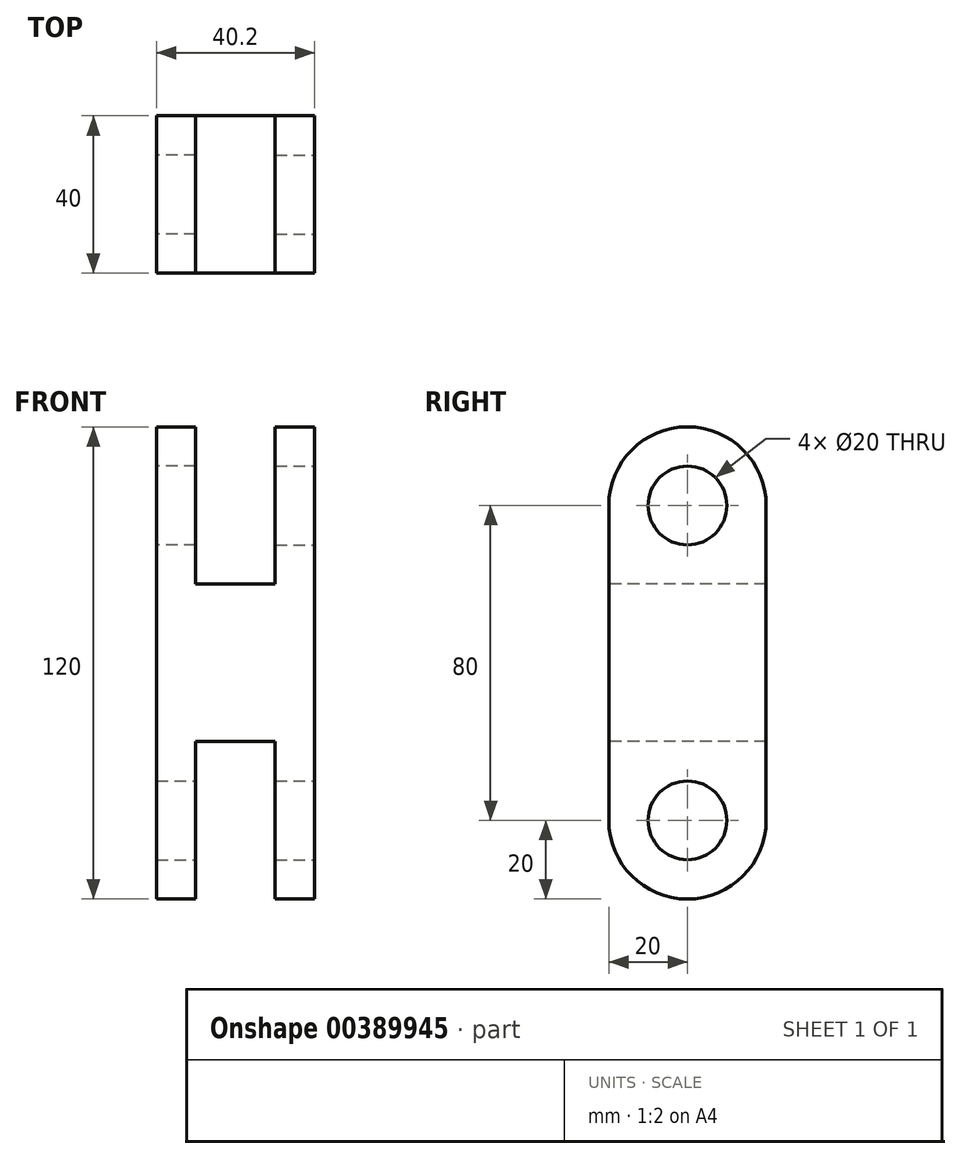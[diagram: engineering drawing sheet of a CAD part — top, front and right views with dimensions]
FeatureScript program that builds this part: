
annotation { "Feature Type Name" : "Feature", "Feature Type Description" : "" }
export const myFeature = defineFeature(function(context is Context, id is Id, definition is map)
    precondition{}
    {
        {
            var Q0;
            Q0=qCreatedBy(makeId("Right.planeOp"),FACE);
            var sketch = newSketch(context, id + "F0", { "sketchPlane" : qUnion([Q0])});
            skLineSegment(sketch, "E0.bottom", {"start": v(20, 40) * mm, "end": v(-20, 40) * mm});
            skLineSegment(sketch, "E0.top", {"start": v(20, -40) * mm, "end": v(-20, -40) * mm});
            skLineSegment(sketch, "E0.left", {"start": v(20, 40) * mm, "end": v(20, -40) * mm});
            skLineSegment(sketch, "E0.right", {"start": v(-20, 40) * mm, "end": v(-20, -40) * mm});
            skPoint(sketch, "E0.middle", {"position": v(0, 0) * mm});
            skSolve(sketch);
        }
        {
            var Q0;
            Q0 = qSketchRegion(id + "F0", true);
            extrude(context, id + "F1", {"entities" : qUnion([Q0]), "depth" : 20.1 * mm});
        }
        {
            var Q0;
            Q0=makeQuery(id+"F1.opExtrude","CAP_FACE",FACE,{"disambiguationData":[OSD([sQuery(id+"F0.wireOp",EDGE,"E0.bottom"),sQuery(id+"F0.wireOp",EDGE,"E0.top"),sQuery(id+"F0.wireOp",EDGE,"E0.left"),sQuery(id+"F0.wireOp",EDGE,"E0.right")])],"isStart":false});
            var sketch = newSketch(context, id + "F2", { "sketchPlane" : qUnion([Q0])});
            skLineSegment(sketch, "E1.bottom", {"start": v(-20, 40) * mm, "end": v(20, 40) * mm});
            skLineSegment(sketch, "E1.left", {"start": v(-20, 40) * mm, "end": v(-20, 60) * mm});
            skLineSegment(sketch, "E1.right", {"start": v(20, 40) * mm, "end": v(20, 60) * mm});
            skArc(sketch, "E2", {"start": v(20, 60) * mm, "mid": v(0, 80) * mm, "end": v(-20, 60) * mm});
            skCircle(sketch, "E3", {"center": v(0, 60) * mm, "radius": 10 * mm});
            skSolve(sketch);
        }
        {
            var Q0;
            Q0 = qSketchRegion(id + "F2", true);
            extrude(context, id + "F3", {"entities" : qUnion([Q0]), "operationType" : NewBodyOperationType.ADD, "oppositeDirection" : true, "depth" : 10 * mm});
        }
        {
            var Q0;
            Q0=makeQuery(id+"F1.opExtrude","SWEPT_BODY",BODY,{"disambiguationData":[OSD([sQuery(id+"F0.wireOp",EDGE,"E0.bottom"),sQuery(id+"F0.wireOp",EDGE,"E0.top"),sQuery(id+"F0.wireOp",EDGE,"E0.left"),sQuery(id+"F0.wireOp",EDGE,"E0.right")])]});
            var Q1;
            Q1=qCreatedBy(makeId("Right.planeOp"),FACE);
            mirror(context, id + "F4", {"operationType" : NewBodyOperationType.ADD, "entities" : qUnion([Q0]), "mirrorPlane" : qUnion([Q1])});
        }
        {
            var Q0;
            {var subQ0=makeQuery(id+"F3.boolean.opBoolean","MERGE",FACE,{"derivedFrom":[makeQuery(id+"F1.opExtrude","SWEPT_FACE",FACE,{"disambiguationData":[OSD([sQuery(id+"F0.wireOp",EDGE,"E0.right")])]}),makeQuery(id+"F3.opExtrude","SWEPT_FACE",FACE,{"disambiguationData":[OSD([sQuery(id+"F2.wireOp",EDGE,"E1.left")])]})]});Q0=makeQuery(id+"F4.boolean.opBoolean","MERGE",FACE,{"derivedFrom":[subQ0,makeQuery(id+"F4.opPattern","COPY",FACE,{"derivedFrom":subQ0,"instanceName":"1"})]});}
            var sketch = newSketch(context, id + "F5", { "sketchPlane" : qUnion([Q0])});
            skLineSegment(sketch, "E4.bottom", {"start": v(-10.1, -40) * mm, "end": v(10.1, -40) * mm});
            skLineSegment(sketch, "E4.top", {"start": v(-10.1, 0) * mm, "end": v(10.1, 0) * mm});
            skLineSegment(sketch, "E4.left", {"start": v(-10.1, -40) * mm, "end": v(-10.1, 0) * mm});
            skLineSegment(sketch, "E4.right", {"start": v(10.1, -40) * mm, "end": v(10.1, 0) * mm});
            skSolve(sketch);
        }
        {
            var Q0;
            Q0 = qSketchRegion(id + "F5", true);
            var Q1;
            {var subQ0=makeQuery(id+"F3.boolean.opBoolean","MERGE",FACE,{"derivedFrom":[makeQuery(id+"F1.opExtrude","SWEPT_FACE",FACE,{"disambiguationData":[OSD([sQuery(id+"F0.wireOp",EDGE,"E0.left")])]}),makeQuery(id+"F3.opExtrude","SWEPT_FACE",FACE,{"disambiguationData":[OSD([sQuery(id+"F2.wireOp",EDGE,"E1.right")])]})]});Q1=makeQuery(id+"F4.boolean.opBoolean","MERGE",FACE,{"derivedFrom":[subQ0,makeQuery(id+"F4.opPattern","COPY",FACE,{"derivedFrom":subQ0,"instanceName":"1"})]});}
            extrude(context, id + "F6", {"entities" : qUnion([Q0]), "operationType" : NewBodyOperationType.REMOVE, "endBound" : BoundingType.UP_TO_SURFACE, "oppositeDirection" : true, "endBoundEntityFace" : qUnion([Q1]), "depth" : 25 * mm});
        }
        {
            var Q0;
            Q0=makeQuery(id+"F3.boolean.opBoolean","MERGE",FACE,{"derivedFrom":[makeQuery(id+"F1.opExtrude","CAP_FACE",FACE,{"disambiguationData":[OSD([sQuery(id+"F0.wireOp",EDGE,"E0.bottom"),sQuery(id+"F0.wireOp",EDGE,"E0.top"),sQuery(id+"F0.wireOp",EDGE,"E0.left"),sQuery(id+"F0.wireOp",EDGE,"E0.right")])],"isStart":false}),makeQuery(id+"F3.opExtrude","CAP_FACE",FACE,{"disambiguationData":[OSD([sQuery(id+"F2.wireOp",EDGE,"E1.bottom"),sQuery(id+"F2.wireOp",EDGE,"E1.left"),sQuery(id+"F2.wireOp",EDGE,"E1.right"),sQuery(id+"F2.wireOp",EDGE,"E2"),sQuery(id+"F2.wireOp",EDGE,"E3")])],"isStart":true})]});
            var sketch = newSketch(context, id + "F7", { "sketchPlane" : qUnion([Q0])});
            skLineSegment(sketch, "E5", {"start": v(0, -40) * mm, "end": v(0, -20) * mm, "construction": true});
            skCircle(sketch, "E6", {"center": v(0, -20) * mm, "radius": 10 * mm});
            skSolve(sketch);
        }
        {
            var Q0;
            Q0 = qSketchRegion(id + "F7", true);
            var Q1;
            Q1=makeQuery(id+"F4.opPattern","COPY",FACE,{"derivedFrom":makeQuery(id+"F3.boolean.opBoolean","MERGE",FACE,{"derivedFrom":[makeQuery(id+"F1.opExtrude","CAP_FACE",FACE,{"disambiguationData":[OSD([sQuery(id+"F0.wireOp",EDGE,"E0.bottom"),sQuery(id+"F0.wireOp",EDGE,"E0.top"),sQuery(id+"F0.wireOp",EDGE,"E0.left"),sQuery(id+"F0.wireOp",EDGE,"E0.right")])],"isStart":false}),makeQuery(id+"F3.opExtrude","CAP_FACE",FACE,{"disambiguationData":[OSD([sQuery(id+"F2.wireOp",EDGE,"E1.bottom"),sQuery(id+"F2.wireOp",EDGE,"E1.left"),sQuery(id+"F2.wireOp",EDGE,"E1.right"),sQuery(id+"F2.wireOp",EDGE,"E2"),sQuery(id+"F2.wireOp",EDGE,"E3")])],"isStart":true})]}),"instanceName":"1"});
            extrude(context, id + "F8", {"entities" : qUnion([Q0]), "operationType" : NewBodyOperationType.REMOVE, "endBound" : BoundingType.UP_TO_SURFACE, "oppositeDirection" : true, "endBoundEntityFace" : qUnion([Q1]), "depth" : 40 * mm});
        }
        {
            var Q0;
            {var subQ1=sQuery(id+"F0.wireOp",EDGE,"E0.left");var subQ3=sQuery(id+"F0.wireOp",EDGE,"E0.top");var subQ6=makeQuery(id+"F1.opExtrude","SWEPT_EDGE",EDGE,{"disambiguationData":[OSD([subQ3,subQ1])]});Q0=makeQuery(id+"F6.boolean.opBoolean","SPLIT",EDGE,{"disambiguationData":[TD([makeQuery(id+"F6.opExtrude","SWEPT_FACE",FACE,{"disambiguationData":[OSD([sQuery(id+"F5.wireOp",EDGE,"E4.right")])]})])],"derivedFrom":makeQuery(id+"F4.boolean.opBoolean","MERGE",EDGE,{"derivedFrom":[subQ6,makeQuery(id+"F4.opPattern","COPY",EDGE,{"derivedFrom":subQ6,"instanceName":"1"})]})});}
            var Q1;
            {var subQ0=sQuery(id+"F0.wireOp",EDGE,"E0.top");var subQ2=sQuery(id+"F0.wireOp",EDGE,"E0.left");var subQ6=makeQuery(id+"F1.opExtrude","SWEPT_EDGE",EDGE,{"disambiguationData":[OSD([subQ0,subQ2])]});Q1=makeQuery(id+"F6.boolean.opBoolean","SPLIT",EDGE,{"disambiguationData":[TD([makeQuery(id+"F6.opExtrude","SWEPT_FACE",FACE,{"disambiguationData":[OSD([sQuery(id+"F5.wireOp",EDGE,"E4.left")])]})])],"derivedFrom":makeQuery(id+"F4.boolean.opBoolean","MERGE",EDGE,{"derivedFrom":[subQ6,makeQuery(id+"F4.opPattern","COPY",EDGE,{"derivedFrom":subQ6,"instanceName":"1"})]})});}
            var Q2;
            {var subQ1=sQuery(id+"F0.wireOp",EDGE,"E0.right");var subQ3=sQuery(id+"F0.wireOp",EDGE,"E0.top");var subQ6=makeQuery(id+"F1.opExtrude","SWEPT_EDGE",EDGE,{"disambiguationData":[OSD([subQ3,subQ1])]});Q2=makeQuery(id+"F6.boolean.opBoolean","SPLIT",EDGE,{"disambiguationData":[TD([makeQuery(id+"F6.opExtrude","SWEPT_FACE",FACE,{"disambiguationData":[OSD([sQuery(id+"F5.wireOp",EDGE,"E4.right")])]})])],"derivedFrom":makeQuery(id+"F4.boolean.opBoolean","MERGE",EDGE,{"derivedFrom":[subQ6,makeQuery(id+"F4.opPattern","COPY",EDGE,{"derivedFrom":subQ6,"instanceName":"1"})]})});}
            var Q3;
            {var subQ0=sQuery(id+"F0.wireOp",EDGE,"E0.top");var subQ4=sQuery(id+"F0.wireOp",EDGE,"E0.right");var subQ6=makeQuery(id+"F1.opExtrude","SWEPT_EDGE",EDGE,{"disambiguationData":[OSD([subQ0,subQ4])]});Q3=makeQuery(id+"F6.boolean.opBoolean","SPLIT",EDGE,{"disambiguationData":[TD([makeQuery(id+"F6.opExtrude","SWEPT_FACE",FACE,{"disambiguationData":[OSD([sQuery(id+"F5.wireOp",EDGE,"E4.left")])]})])],"derivedFrom":makeQuery(id+"F4.boolean.opBoolean","MERGE",EDGE,{"derivedFrom":[subQ6,makeQuery(id+"F4.opPattern","COPY",EDGE,{"derivedFrom":subQ6,"instanceName":"1"})]})});}
            fillet(context, id + "F9", {"entities" : qUnion([Q0, Q1, Q2, Q3]), "radius" : 20 * mm, "tangentPropagation" : true, "allowEdgeOverflow" : false});
        }
    });
